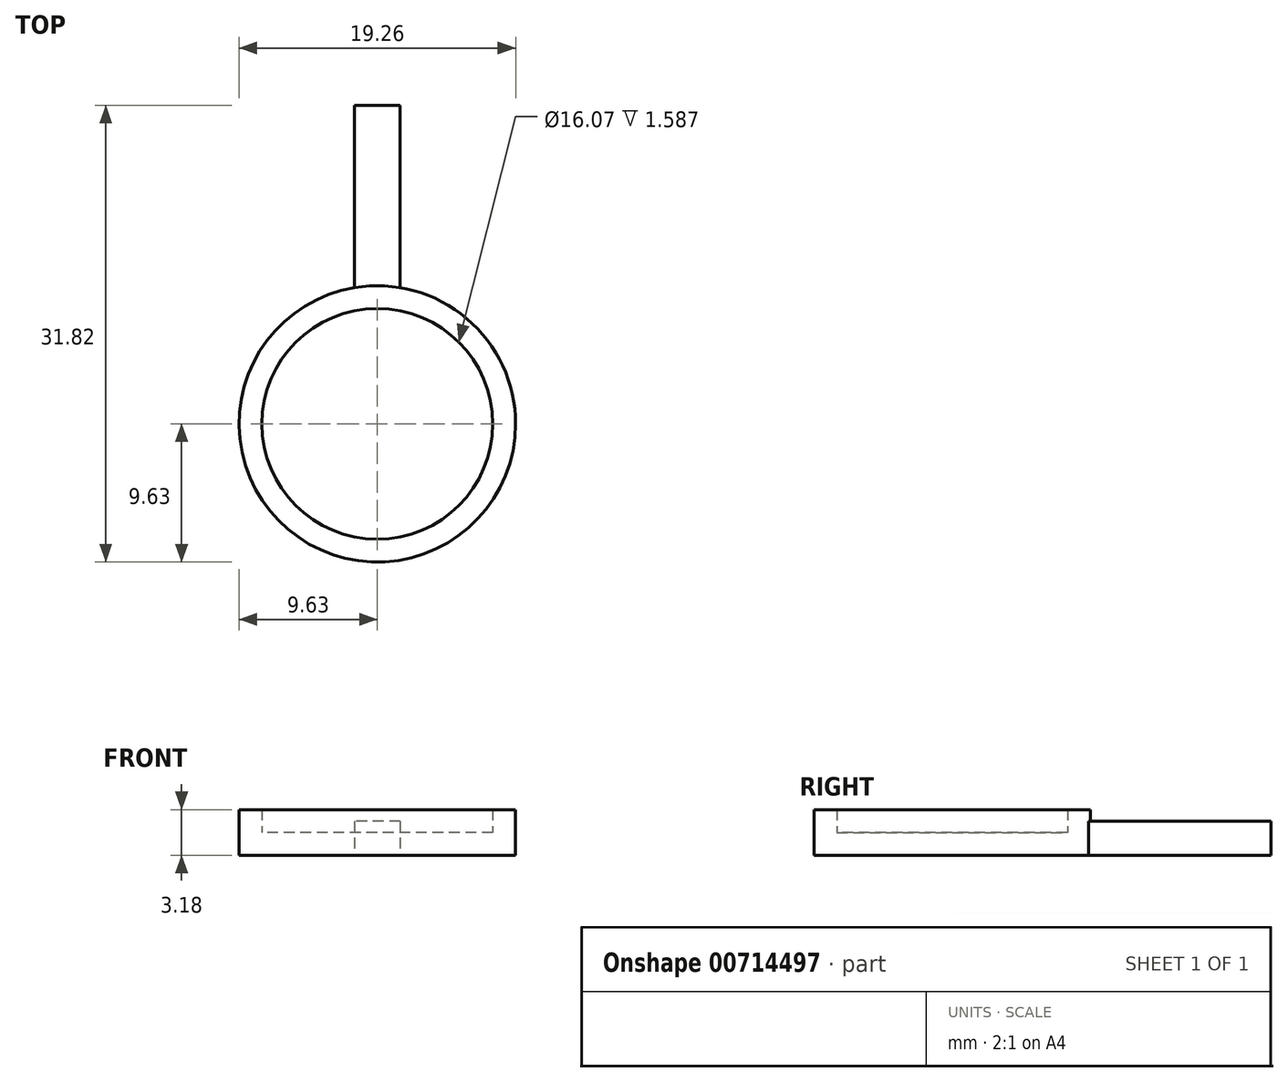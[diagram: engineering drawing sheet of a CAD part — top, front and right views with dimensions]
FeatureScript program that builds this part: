
annotation { "Feature Type Name" : "Feature", "Feature Type Description" : "" }
export const myFeature = defineFeature(function(context is Context, id is Id, definition is map)
    precondition{}
    {
        {
            var Q0;
            Q0=qCreatedBy(makeId("Top.planeOp"),FACE);
            var sketch = newSketch(context, id + "F0", { "sketchPlane" : qUnion([Q0])});
            skCircle(sketch, "E0", {"center": v(0, 0) * mm, "radius": 9.62 * mm});
            skSolve(sketch);
        }
        {
            var Q0;
            Q0=qSketchRegion(id+"F0",true);
            extrude(context, id + "F1", {"entities" : qUnion([Q0]), "depth" : 1.59 * mm, "offsetDistance" : 25.4 * mm});
        }
        {
            var Q0;
            Q0=makeQuery(id+"F1.opExtrude","CAP_FACE",FACE,{"disambiguationData":[OSD([sQuery(id+"F0.wireOp",EDGE,"E0")])],"isStart":false});
            var sketch = newSketch(context, id + "F2", { "sketchPlane" : qUnion([Q0])});
            skCircle(sketch, "E1.0.0", {"center": v(0, 0) * mm, "radius": 9.62 * mm});
            skCircle(sketch, "E2.0", {"center": v(0, 0) * mm, "radius": 8.04 * mm});
            skSolve(sketch);
        }
        {
            var Q0;
            Q0=makeQuery(id+"F2.imprint","IMPRINT",FACE,{"disambiguationData":[TD([[makeQuery(id+"F2.imprint","IMPRINT",EDGE,{"derivedFrom":sQuery(id+"F2.wireOp",EDGE,"E1.0.0")}),1.0]])]});
            extrude(context, id + "F3", {"entities" : qUnion([Q0]), "operationType" : NewBodyOperationType.ADD, "depth" : 1.59 * mm, "offsetDistance" : 25.4 * mm});
        }
        {
            var Q0;
            Q0=qCreatedBy(makeId("Top.planeOp"),FACE);
            var sketch = newSketch(context, id + "F4", { "sketchPlane" : qUnion([Q0])});
            skLineSegment(sketch, "E3.bottom", {"start": v(1.59, 9.5) * mm, "end": v(-1.59, 9.5) * mm});
            skLineSegment(sketch, "E3.top", {"start": v(1.59, 22.2) * mm, "end": v(-1.59, 22.2) * mm});
            skLineSegment(sketch, "E3.left", {"start": v(1.59, 9.5) * mm, "end": v(1.59, 22.2) * mm});
            skLineSegment(sketch, "E3.right", {"start": v(-1.59, 9.5) * mm, "end": v(-1.59, 22.2) * mm});
            skPoint(sketch, "E3.middle", {"position": v(0, 15.84) * mm});
            skSolve(sketch);
        }
        {
            var Q0;
            Q0=qSketchRegion(id+"F4",true);
            var Q1;
            Q1=makeQuery(id+"F3.opExtrude","CAP_FACE",FACE,{"disambiguationData":[OSD([sQuery(id+"F2.wireOp",EDGE,"E1.0.0"),sQuery(id+"F2.wireOp",EDGE,"E2.0")])],"isStart":false});
            extrude(context, id + "F5", {"entities" : qUnion([Q0]), "operationType" : NewBodyOperationType.ADD, "depth" : 2.38 * mm, "endBoundEntityFace" : qUnion([Q1]), "hasOffset" : true, "offsetDistance" : 1 * mm});
        }
    });
